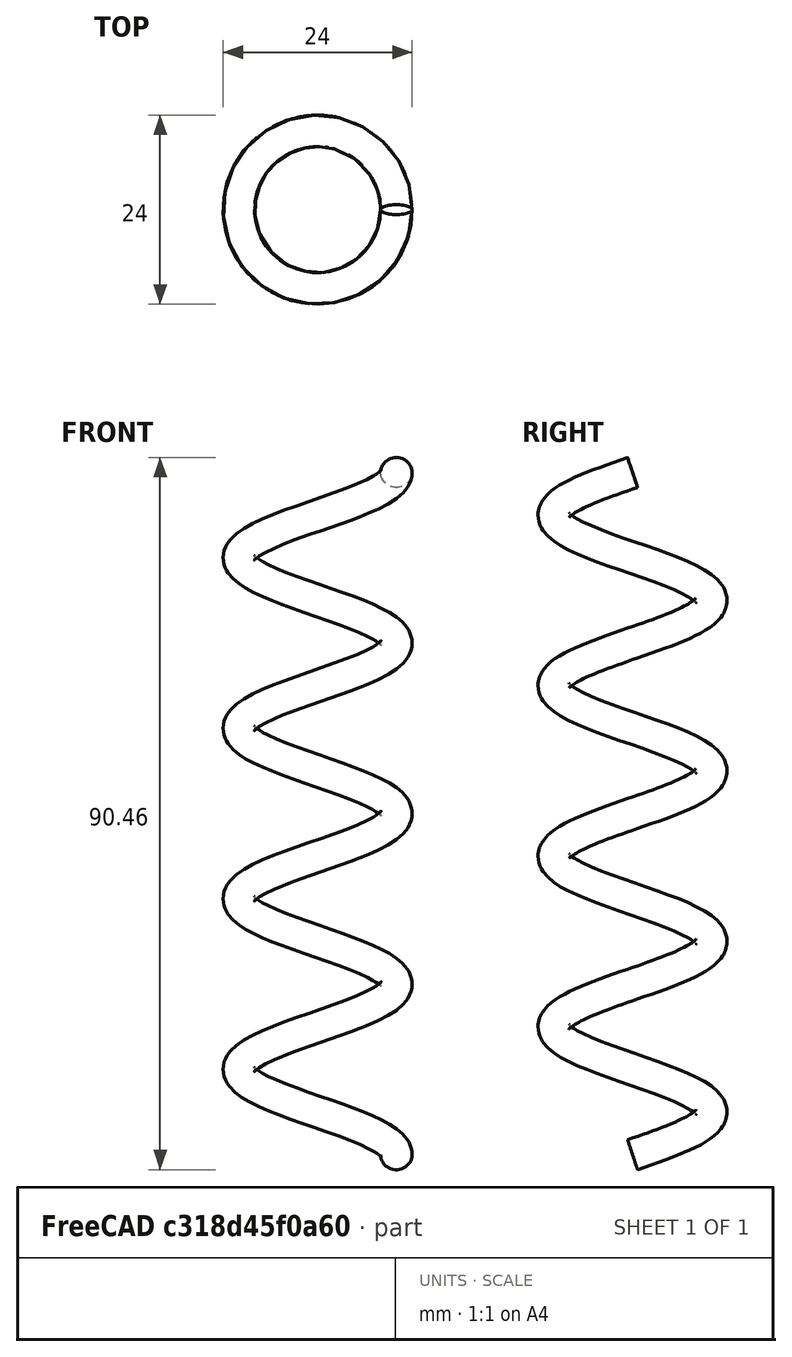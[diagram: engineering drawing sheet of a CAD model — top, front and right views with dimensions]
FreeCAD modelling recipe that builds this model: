
FCSTD DOCUMENT  (FreeCAD 0.18.2R)
Label: 208 - stretching the spring 
License: All rights reserved
LicenseURL: http://en.wikipedia.org/wiki/All_rights_reserved
objects: Part::Helix×1, Part::Circle×1, Part::Sweep×1, App::DocumentObjectGroupPython×1, Spreadsheet::Sheet×1
note: 3 computed .brp shape members not serialized (recipe doc carries the construction recipe); baked Part::Feature solids carry a one-line shape summary decoded from their .brp

FEATURE [Part::Helix] Helix
  Angle = 0
  AttacherType = Attacher::AttachEngine3D
  Height = 86.6667
  LocalCoord = 0
  Pitch = 21.6667
  Radius = 10
  Style = 1
  expr: Height = Spreadsheet.height
  expr: Pitch = Spreadsheet.step
FEATURE [Part::Circle] Circle
  Angle0 = 0
  Angle1 = 360
  AttacherType = Attacher::AttachEngine3D
  Placement = pos=(10,0,0) rot=(1,0,0;5.03414rad)
  Radius = 2
  expr: Placement.Rotation.Angle = Spreadsheet.angle
FEATURE [Part::Sweep] Sweep
  Frenet = true
  Sections = -> [Circle]
  Solid = true
  Spine = -> Helix
  Transition = 1
FEATURE [App::DocumentObjectGroupPython] My_Manager  # scripted group (container) (typed FeaturePython)
  intervall = 100
  sleeptime = 0.02
  start = 0
  step = 100
  text = NO
FEATURE [Spreadsheet::Sheet] Spreadsheet
  cells = A1=step; B1(step)==5 * (1 + C1 / 30); C1==My_Manager.step; A2=height; B2(height)==20 * (1 + C1 / 30); A3=angle; B3(angle)==274.7 * (1 + C1 / 2000)
